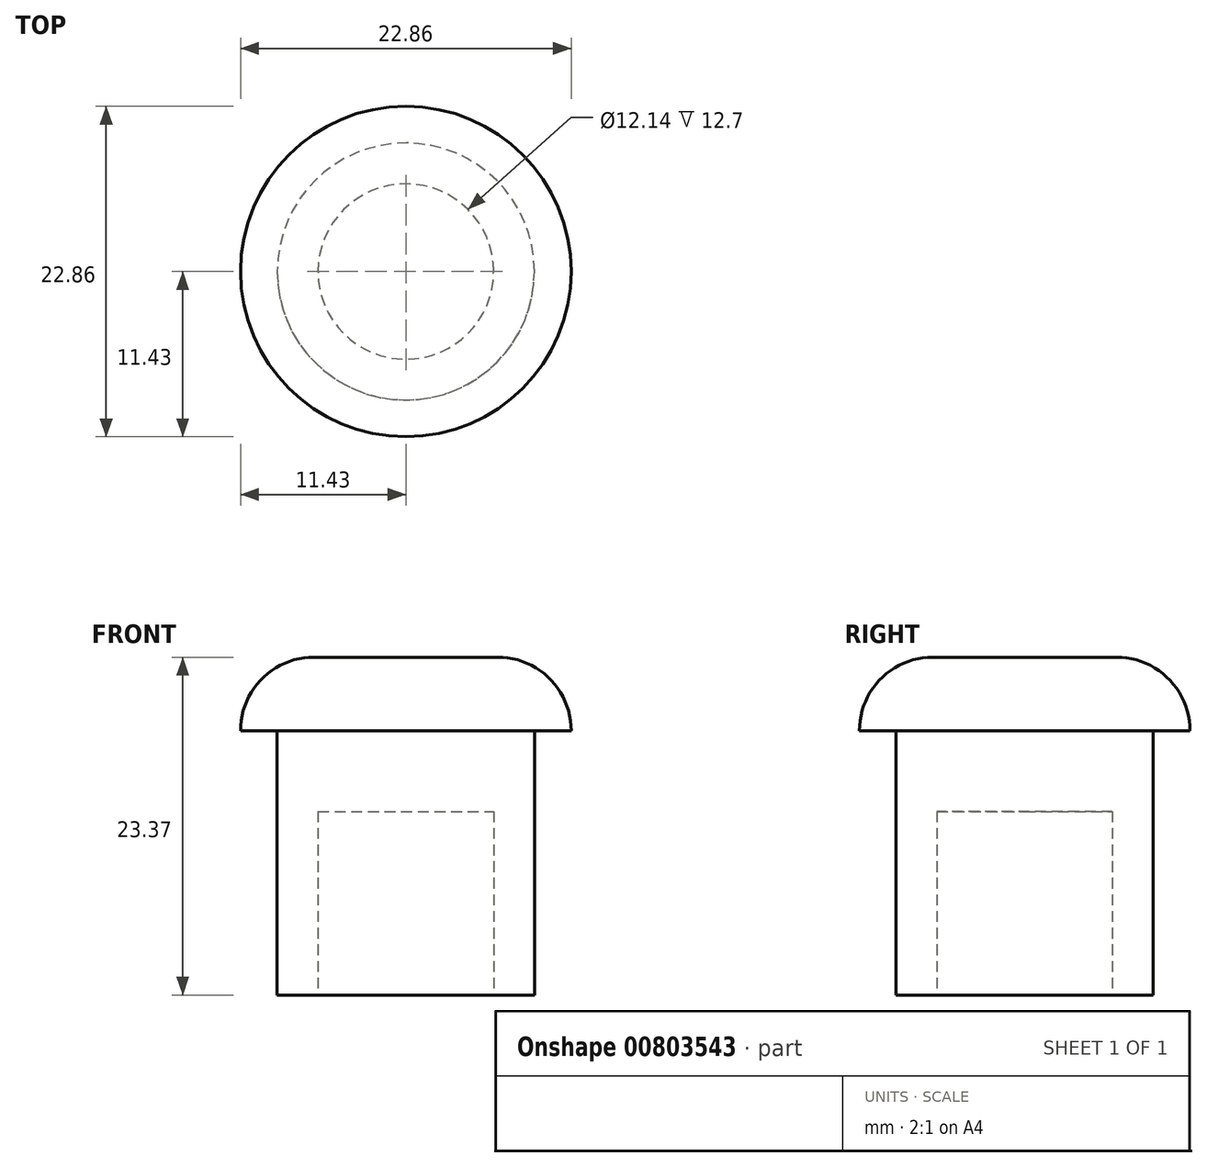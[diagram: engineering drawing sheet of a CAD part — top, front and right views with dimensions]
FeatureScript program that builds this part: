
annotation { "Feature Type Name" : "Feature", "Feature Type Description" : "" }
export const myFeature = defineFeature(function(context is Context, id is Id, definition is map)
    precondition{}
    {
        {
            var Q0;
            Q0=qCreatedBy(makeId("Top.planeOp"),FACE);
            var sketch = newSketch(context, id + "F0", { "sketchPlane" : qUnion([Q0])});
            skCircle(sketch, "E0", {"center": v(0, 0) * mm, "radius": 11.43 * mm});
            skSolve(sketch);
        }
        {
            var Q0;
            Q0 = qSketchRegion(id + "F0", true);
            extrude(context, id + "F1", {"entities" : qUnion([Q0]), "depth" : 5.08 * mm, "offsetDistance" : 25.4 * mm});
        }
        {
            var Q0;
            Q0=makeQuery(id+"F1.opExtrude","CAP_EDGE",EDGE,{"disambiguationData":[OSD([sQuery(id+"F0.wireOp",EDGE,"E0")])],"isStart":false});
            fillet(context, id + "F2", {"entities" : qUnion([Q0]), "radius" : 5.08 * mm, "tangentPropagation" : true, "allowEdgeOverflow" : false});
        }
        {
            var Q0;
            Q0=makeQuery(id+"F1.opExtrude","CAP_FACE",FACE,{"disambiguationData":[OSD([sQuery(id+"F0.wireOp",EDGE,"E0")])],"isStart":true});
            var sketch = newSketch(context, id + "F3", { "sketchPlane" : qUnion([Q0])});
            skCircle(sketch, "E1", {"center": v(0, 0) * mm, "radius": 8.9 * mm});
            skSolve(sketch);
        }
        {
            var Q0;
            Q0 = qSketchRegion(id + "F3", true);
            extrude(context, id + "F4", {"entities" : qUnion([Q0]), "operationType" : NewBodyOperationType.ADD, "depth" : 18.29 * mm, "offsetDistance" : 25.4 * mm});
        }
        {
            var Q0;
            Q0=makeQuery(id+"F4.opExtrude","CAP_FACE",FACE,{"disambiguationData":[OSD([sQuery(id+"F3.wireOp",EDGE,"E1")])],"isStart":false});
            var sketch = newSketch(context, id + "F5", { "sketchPlane" : qUnion([Q0])});
            skCircle(sketch, "E2", {"center": v(0, 0) * mm, "radius": 6.07 * mm});
            skSolve(sketch);
        }
        {
            var Q0;
            Q0=makeQuery(id+"F5.imprint","IMPRINT",FACE,{"disambiguationData":[TD([[makeQuery(id+"F5.imprint","IMPRINT",EDGE,{"derivedFrom":sQuery(id+"F5.wireOp",EDGE,"E2")}),1.0]])]});
            extrude(context, id + "F6", {"entities" : qUnion([Q0]), "operationType" : NewBodyOperationType.REMOVE, "oppositeDirection" : true, "depth" : 12.7 * mm, "offsetDistance" : 25.4 * mm});
        }
    });
